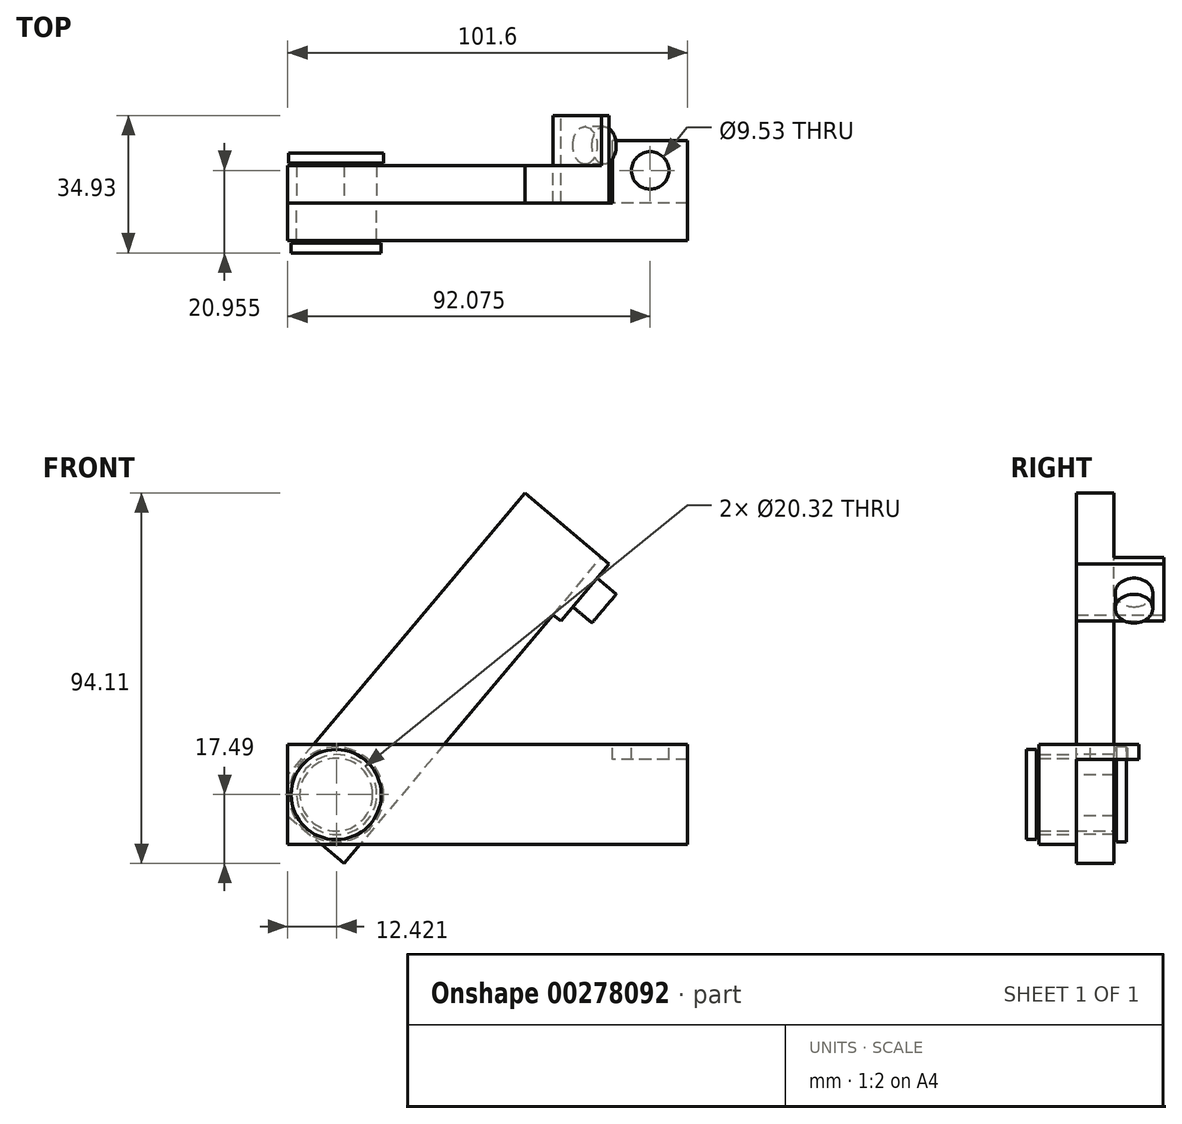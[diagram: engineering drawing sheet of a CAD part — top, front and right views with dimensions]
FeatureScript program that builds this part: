
annotation { "Feature Type Name" : "Feature", "Feature Type Description" : "" }
export const myFeature = defineFeature(function(context is Context, id is Id, definition is map)
    precondition{}
    {
        {
            var Q0;
            Q0=qCreatedBy(makeId("Front.planeOp"),FACE);
            var sketch = newSketch(context, id + "F0", { "sketchPlane" : qUnion([Q0])});
            skLineSegment(sketch, "E0.bottom", {"start": v(-50.8, 12.7) * mm, "end": v(50.8, 12.7) * mm});
            skLineSegment(sketch, "E0.top", {"start": v(-50.8, -12.7) * mm, "end": v(50.8, -12.7) * mm});
            skLineSegment(sketch, "E0.right", {"start": v(50.8, 12.7) * mm, "end": v(50.8, -12.7) * mm});
            skPoint(sketch, "E0.middle", {"position": v(0, 0) * mm});
            skCircle(sketch, "E1", {"center": v(-38.38, 0) * mm, "radius": 10.16 * mm});
            skLineSegment(sketch, "E2", {"start": v(9.44, 76.62) * mm, "end": v(-55.94, -1.15) * mm});
            skLineSegment(sketch, "E3", {"start": v(28.88, 60.28) * mm, "end": v(-36.5, -17.5) * mm});
            skLineSegment(sketch, "E4", {"start": v(-55.77, -1.29) * mm, "end": v(-36.33, -17.63) * mm});
            skLineSegment(sketch, "E5", {"start": v(9.44, 76.62) * mm, "end": v(28.88, 60.28) * mm});
            skLineSegment(sketch, "E6", {"start": v(-50.8, 12.7) * mm, "end": v(-50.8, -12.7) * mm});
            skCircle(sketch, "E7", {"center": v(9.8, 68.45) * mm, "radius": 3.43 * mm});
            skPoint(sketch, "E7.centerSnap0", {"position": v(19.16, 68.45) * mm});
            skSolve(sketch);
        }
        {
            var Q0;
            {var subQ0=sQuery(id+"F0.wireOp",EDGE,"E4");var subQ1=sQuery(id+"F0.wireOp",EDGE,"E0.top");var subQ2=makeQuery(id+"F0.imprint","INTERSECT",VERTEX,{"derivedFrom":[subQ1,subQ0]});Q0=makeQuery(id+"F0.imprint","IMPRINT",FACE,{"disambiguationData":[TD([[makeQuery(id+"F0.imprint","IMPRINT",EDGE,{"disambiguationData":[TD([[subQ2,-1.0]])],"derivedFrom":subQ1}),-1.0]])]});}
            var Q1;
            Q1=makeQuery(id+"F0.imprint","IMPRINT",FACE,{"disambiguationData":[TD([[makeQuery(id+"F0.imprint","IMPRINT",EDGE,{"derivedFrom":sQuery(id+"F0.wireOp",EDGE,"E1")}),-1.0]])]});
            var Q2;
            {var subQ5=sQuery(id+"F0.wireOp",EDGE,"E5");Q2=makeQuery(id+"F0.imprint","IMPRINT",FACE,{"disambiguationData":[TD([[makeQuery(id+"F0.imprint","IMPRINT",EDGE,{"derivedFrom":subQ5}),-1.0]])]});}
            var Q3;
            Q3=makeQuery(id+"F0.imprint","IMPRINT",FACE,{"disambiguationData":[TD([[makeQuery(id+"F0.imprint","IMPRINT",EDGE,{"derivedFrom":sQuery(id+"F0.wireOp",EDGE,"E7")}),1.0]])]});
            extrude(context, id + "F1", {"entities" : qUnion([Q0, Q1, Q2, Q3]), "oppositeDirection" : true, "depth" : 9.52 * mm});
        }
        {
            var Q0;
            {var subQ0=sQuery(id+"F0.wireOp",EDGE,"E0.right");Q0=makeQuery(id+"F0.imprint","IMPRINT",FACE,{"disambiguationData":[TD([[makeQuery(id+"F0.imprint","IMPRINT",EDGE,{"derivedFrom":subQ0}),-1.0]])]});}
            var Q1;
            Q1=makeQuery(id+"F0.imprint","IMPRINT",FACE,{"disambiguationData":[TD([[makeQuery(id+"F0.imprint","IMPRINT",EDGE,{"derivedFrom":sQuery(id+"F0.wireOp",EDGE,"E1")}),-1.0]])]});
            var Q2;
            {var subQ0=sQuery(id+"F0.wireOp",EDGE,"E6");var subQ1=sQuery(id+"F0.wireOp",EDGE,"E0.bottom");var subQ2=makeQuery(id+"F0.imprint","INTERSECT",VERTEX,{"derivedFrom":[subQ1,subQ0]});Q2=makeQuery(id+"F0.imprint","IMPRINT",FACE,{"disambiguationData":[TD([[makeQuery(id+"F0.imprint","IMPRINT",EDGE,{"disambiguationData":[TD([[subQ2,-1.0]])],"derivedFrom":subQ1}),-1.0]])]});}
            var Q3;
            {var subQ0=sQuery(id+"F0.wireOp",EDGE,"E6");var subQ1=sQuery(id+"F0.wireOp",EDGE,"E0.top");var subQ2=makeQuery(id+"F0.imprint","INTERSECT",VERTEX,{"derivedFrom":[subQ1,subQ0]});Q3=makeQuery(id+"F0.imprint","IMPRINT",FACE,{"disambiguationData":[TD([[makeQuery(id+"F0.imprint","IMPRINT",EDGE,{"disambiguationData":[TD([[subQ2,-1.0]])],"derivedFrom":subQ1}),1.0]])]});}
            extrude(context, id + "F2", {"entities" : qUnion([Q0, Q1, Q2, Q3]), "depth" : 9.52 * mm});
        }
        {
            var Q0;
            Q0=makeQuery(id+"F2.opExtrude","SWEPT_FACE",FACE,{"disambiguationData":[OSD([sQuery(id+"F0.wireOp",EDGE,"E0.bottom")])]});
            var sketch = newSketch(context, id + "F3", { "sketchPlane" : qUnion([Q0])});
            skLineSegment(sketch, "E8.bottom", {"start": v(50.8, -9.53) * mm, "end": v(31.75, -9.53) * mm});
            skLineSegment(sketch, "E8.top", {"start": v(50.8, 15.88) * mm, "end": v(31.75, 15.88) * mm});
            skLineSegment(sketch, "E8.left", {"start": v(50.8, -9.52) * mm, "end": v(50.8, 15.88) * mm});
            skLineSegment(sketch, "E8.right", {"start": v(31.75, -9.53) * mm, "end": v(31.75, 15.87) * mm});
            skCircle(sketch, "E9", {"center": v(41.28, 8.26) * mm, "radius": 4.76 * mm});
            skPoint(sketch, "E9.centerSnap0", {"position": v(41.28, -9.53) * mm});
            skSolve(sketch);
        }
        {
            var Q0;
            Q0 = qSketchRegion(id + "F3", true);
            extrude(context, id + "F4", {"entities" : qUnion([Q0]), "operationType" : NewBodyOperationType.ADD, "oppositeDirection" : true, "depth" : 3.8 * mm});
        }
        {
            var Q0;
            Q0=qCreatedBy(makeId("Front.planeOp"),FACE);
            var sketch = newSketch(context, id + "F5", { "sketchPlane" : qUnion([Q0])});
            skCircle(sketch, "E10", {"center": v(-38.5, 0) * mm, "radius": 9.26 * mm});
            skCircle(sketch, "E11", {"center": v(-38.5, 0) * mm, "radius": 13.48 * mm});
            skSolve(sketch);
        }
        {
            var Q0;
            Q0=makeQuery(id+"F5.imprint","IMPRINT",FACE,{"disambiguationData":[TD([[makeQuery(id+"F5.imprint","IMPRINT",EDGE,{"derivedFrom":sQuery(id+"F5.wireOp",EDGE,"E10")}),1.0]])]});
            var Q1;
            Q1=sQuery(id+"F5.wireOp",EDGE,"E10");
            extrude(context, id + "F6", {"entities" : qUnion([Q0]), "surfaceEntities" : qUnion([Q1]), "endBound" : BoundingType.SYMMETRIC, "depth" : 20.32 * mm});
        }
        {
            var Q0;
            Q0=makeQuery(id+"F6.opExtrude","CAP_FACE",FACE,{"disambiguationData":[OSD([sQuery(id+"F5.wireOp",EDGE,"E10")])],"isStart":true});
            var sketch = newSketch(context, id + "F7", { "sketchPlane" : qUnion([Q0])});
            skCircle(sketch, "E12", {"center": v(38.5, 0) * mm, "radius": 12.06 * mm});
            skSolve(sketch);
        }
        {
            var Q0;
            Q0 = qSketchRegion(id + "F7", true);
            extrude(context, id + "F8", {"entities" : qUnion([Q0]), "operationType" : NewBodyOperationType.ADD, "depth" : 2.54 * mm});
        }
        {
            var Q0;
            Q0=makeQuery(id+"F6.opExtrude","CAP_FACE",FACE,{"disambiguationData":[OSD([sQuery(id+"F5.wireOp",EDGE,"E10")])],"isStart":false});
            var sketch = newSketch(context, id + "F9", { "sketchPlane" : qUnion([Q0])});
            skCircle(sketch, "E13", {"center": v(-38.5, 0) * mm, "radius": 11.43 * mm});
            skSolve(sketch);
        }
        {
            var Q0;
            Q0 = qSketchRegion(id + "F9", true);
            extrude(context, id + "F10", {"entities" : qUnion([Q0]), "operationType" : NewBodyOperationType.ADD, "depth" : 2.54 * mm});
        }
        {
            var Q0;
            Q0=makeQuery(id+"F1.opExtrude","SWEPT_FACE",FACE,{"disambiguationData":[OSD([sQuery(id+"F0.wireOp",EDGE,"E3")])]});
            var sketch = newSketch(context, id + "F11", { "sketchPlane" : qUnion([Q0])});
            skLineSegment(sketch, "E14.bottom", {"start": v(0, 64.73) * mm, "end": v(22.23, 64.73) * mm});
            skLineSegment(sketch, "E14.top", {"start": v(0, 45.68) * mm, "end": v(22.23, 45.68) * mm});
            skLineSegment(sketch, "E14.left", {"start": v(0, 64.73) * mm, "end": v(0, 45.68) * mm});
            skLineSegment(sketch, "E14.right", {"start": v(22.23, 64.73) * mm, "end": v(22.23, 45.68) * mm});
            skSolve(sketch);
        }
        {
            var Q0;
            {var subQ0=sQuery(id+"F11.wireOp",EDGE,"E14.left");Q0=makeQuery(id+"F11.imprint","IMPRINT",FACE,{"disambiguationData":[TD([[makeQuery(id+"F11.imprint","IMPRINT",EDGE,{"derivedFrom":subQ0}),1.0]])]});}
            extrude(context, id + "F12", {"entities" : qUnion([Q0]), "operationType" : NewBodyOperationType.ADD, "depth" : 2.54 * mm});
        }
        {
            var Q0;
            Q0 = qSketchRegion(id + "F11", true);
            extrude(context, id + "F13", {"entities" : qUnion([Q0]), "operationType" : NewBodyOperationType.ADD, "depth" : 2.54 * mm});
        }
        {
            var Q0;
            {var subQ0=sQuery(id+"F11.wireOp",EDGE,"E14.left");var subQ1=sQuery(id+"F11.wireOp",EDGE,"E14.top");var subQ2=sQuery(id+"F11.wireOp",EDGE,"E14.bottom");Q0=makeQuery(id+"F13.boolean.opBoolean","MERGE",FACE,{"derivedFrom":[makeQuery(id+"F12.opExtrude","CAP_FACE",FACE,{"disambiguationData":[OSD([sQuery(id+"F0.wireOp",EDGE,"E3"),subQ2,subQ1,subQ0])],"isStart":false}),makeQuery(id+"F13.opExtrude","CAP_FACE",FACE,{"disambiguationData":[OSD([subQ2,subQ1,subQ0,sQuery(id+"F11.wireOp",EDGE,"E14.right")])],"isStart":false})]});}
            var sketch = newSketch(context, id + "F14", { "sketchPlane" : qUnion([Q0])});
            skCircle(sketch, "E15", {"center": v(14.6, 55.2) * mm, "radius": 4.76 * mm});
            skSolve(sketch);
        }
        {
            var Q0;
            Q0 = qSketchRegion(id + "F14", true);
            extrude(context, id + "F15", {"entities" : qUnion([Q0]), "operationType" : NewBodyOperationType.ADD, "depth" : 6.35 * mm});
        }
    });
